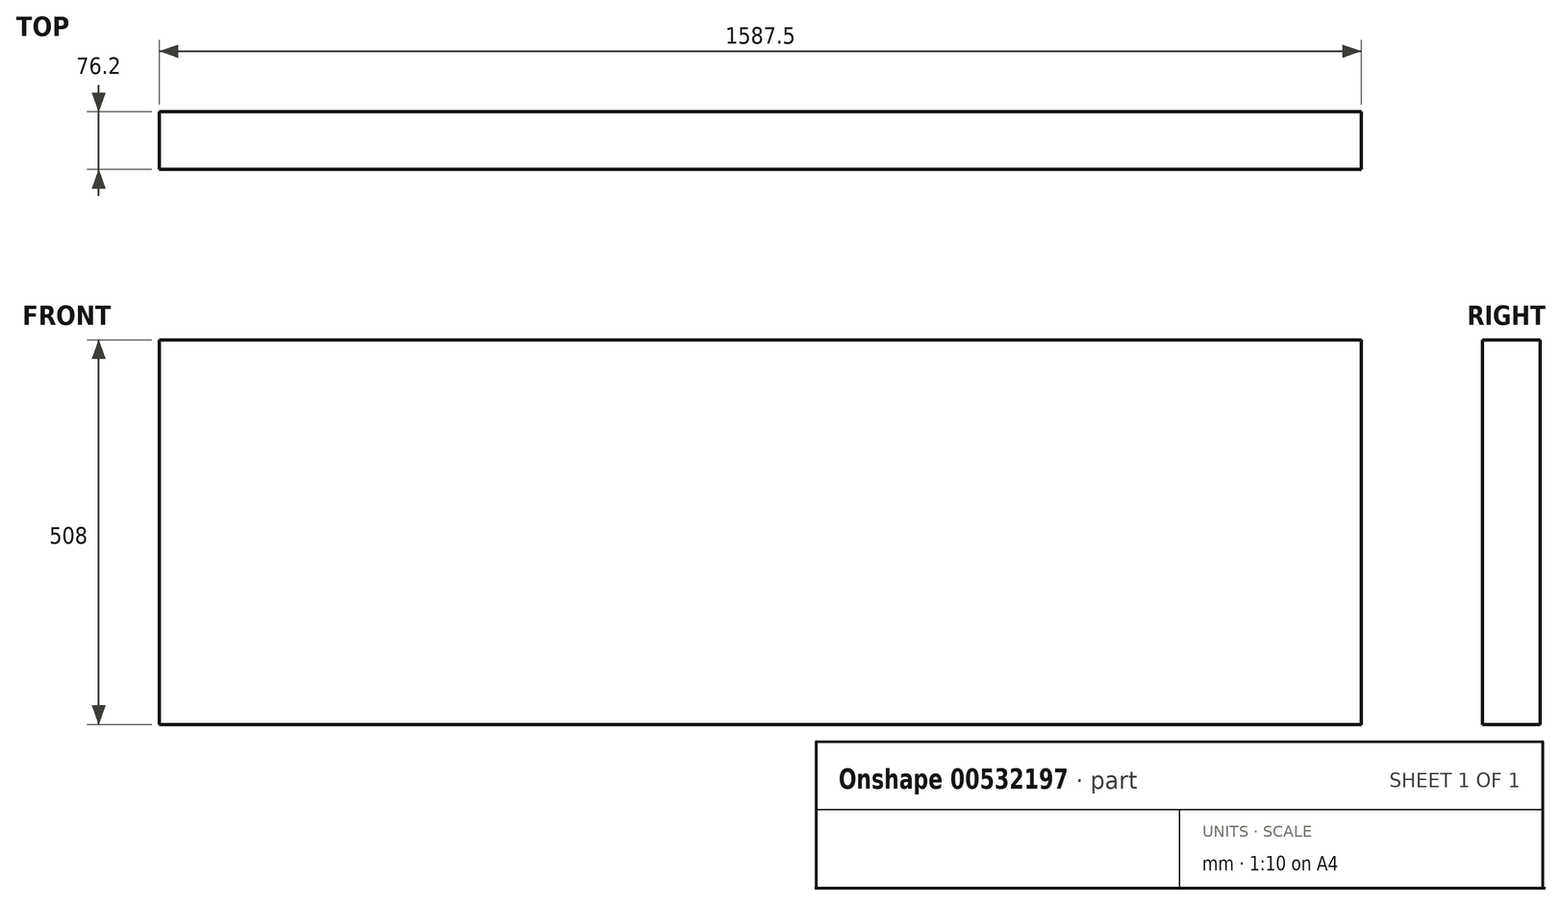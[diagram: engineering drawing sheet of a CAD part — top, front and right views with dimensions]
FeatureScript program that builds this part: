
annotation { "Feature Type Name" : "Feature", "Feature Type Description" : "" }
export const myFeature = defineFeature(function(context is Context, id is Id, definition is map)
    precondition{}
    {
        {
            var Q0;
            Q0=qCreatedBy(makeId("Front.planeOp"),FACE);
            var sketch = newSketch(context, id + "F0", { "sketchPlane" : qUnion([Q0])});
            skLineSegment(sketch, "E0.bottom", {"start": v(793.75, 254) * mm, "end": v(-793.75, 254) * mm});
            skLineSegment(sketch, "E0.top", {"start": v(793.75, -254) * mm, "end": v(-793.75, -254) * mm});
            skLineSegment(sketch, "E0.left", {"start": v(793.75, 254) * mm, "end": v(793.75, -254) * mm});
            skLineSegment(sketch, "E0.right", {"start": v(-793.75, 254) * mm, "end": v(-793.75, -254) * mm});
            skPoint(sketch, "E0.middle", {"position": v(0, 0) * mm});
            skSolve(sketch);
        }
        {
            var Q0;
            Q0 = qSketchRegion(id + "F0", true);
            extrude(context, id + "F1", {"entities" : qUnion([Q0]), "depth" : 76.2 * mm, "offsetDistance" : 25.4 * mm});
        }
    });
